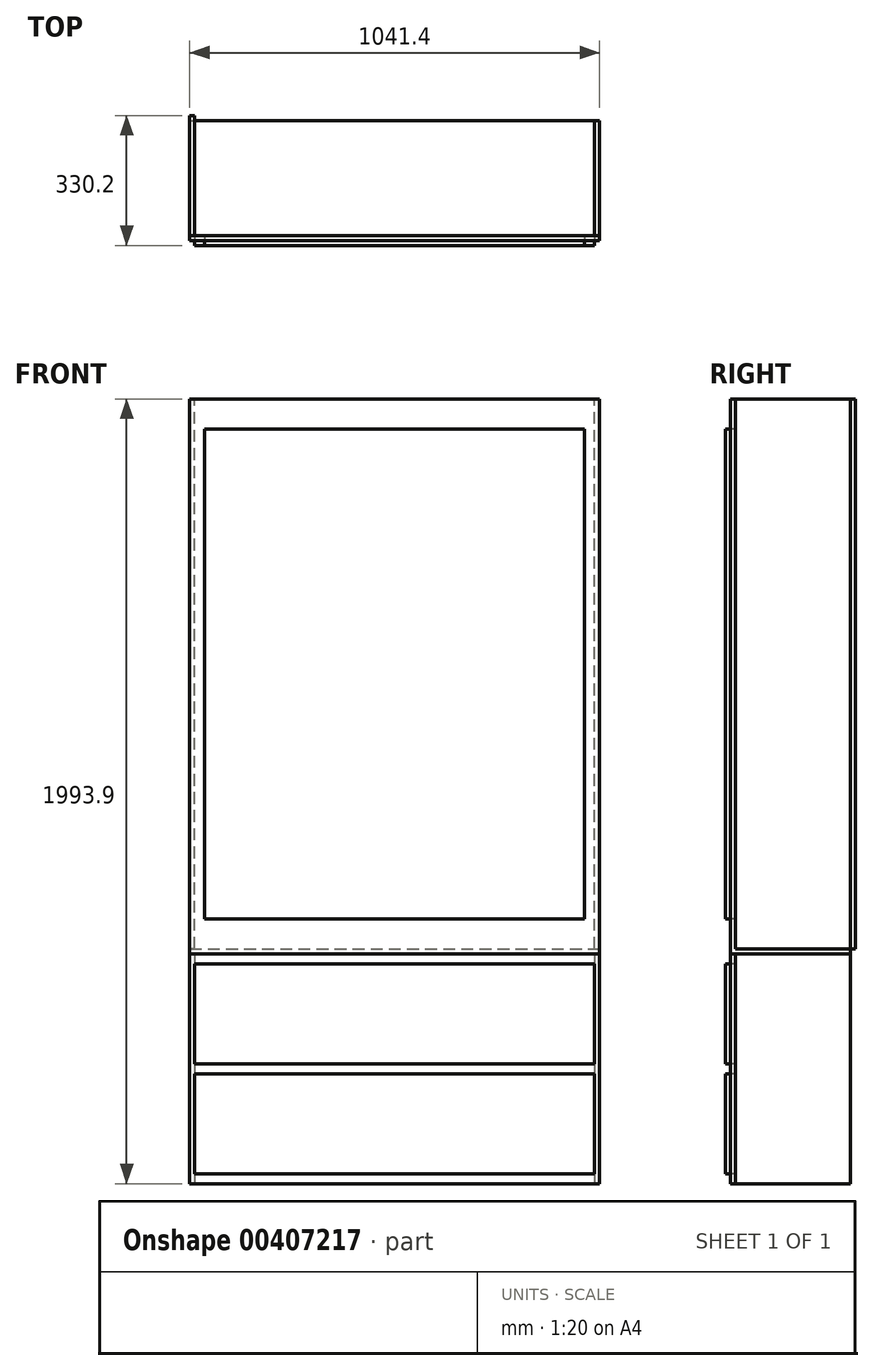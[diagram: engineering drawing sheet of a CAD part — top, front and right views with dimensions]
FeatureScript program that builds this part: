
annotation { "Feature Type Name" : "Feature", "Feature Type Description" : "" }
export const myFeature = defineFeature(function(context is Context, id is Id, definition is map)
    precondition{}
    {
        {
            var Q0;
            Q0=qCreatedBy(makeId("Front.planeOp"),FACE);
            var sketch = newSketch(context, id + "F0", { "sketchPlane" : qUnion([Q0])});
            skLineSegment(sketch, "E0.bottom", {"start": v(0, 839) * mm, "end": v(-482.6, 839) * mm});
            skLineSegment(sketch, "E0.top", {"start": v(0, -405.6) * mm, "end": v(-482.6, -405.6) * mm});
            skLineSegment(sketch, "E0.left", {"start": v(0, 839) * mm, "end": v(0, -405.6) * mm});
            skLineSegment(sketch, "E0.right", {"start": v(-482.6, 839) * mm, "end": v(-482.6, -405.6) * mm});
            skSolve(sketch);
        }
        {
            var Q0;
            Q0=makeQuery(id+"F0.imprint","IMPRINT",FACE,{"disambiguationData":[TD([[makeQuery(id+"F0.imprint","IMPRINT",EDGE,{"derivedFrom":sQuery(id+"F0.wireOp",EDGE,"E0.bottom")}),1.0]])]});
            extrude(context, id + "F1", {"entities" : qUnion([Q0]), "depth" : 12.7 * mm});
        }
        {
            var Q0;
            Q0=qCreatedBy(makeId("Front.planeOp"),FACE);
            var sketch = newSketch(context, id + "F2", { "sketchPlane" : qUnion([Q0])});
            skLineSegment(sketch, "E1.bottom", {"start": v(122.25, 18.6) * mm, "end": v(1138.25, 18.6) * mm});
            skLineSegment(sketch, "E1.top", {"start": v(122.25, -311.6) * mm, "end": v(1138.25, -311.6) * mm});
            skLineSegment(sketch, "E1.left", {"start": v(122.25, 18.6) * mm, "end": v(122.25, -311.6) * mm});
            skLineSegment(sketch, "E1.right", {"start": v(1138.25, 18.6) * mm, "end": v(1138.25, -311.6) * mm});
            skSolve(sketch);
        }
        {
            var Q0;
            Q0=makeQuery(id+"F2.imprint","IMPRINT",FACE,{"disambiguationData":[TD([[makeQuery(id+"F2.imprint","IMPRINT",EDGE,{"derivedFrom":sQuery(id+"F2.wireOp",EDGE,"E1.bottom")}),-1.0]])]});
            extrude(context, id + "F3", {"entities" : qUnion([Q0]), "depth" : 12.7 * mm});
        }
        {
            var Q0;
            Q0=qCreatedBy(makeId("Front.planeOp"),FACE);
            var sketch = newSketch(context, id + "F4", { "sketchPlane" : qUnion([Q0])});
            skLineSegment(sketch, "E2.bottom", {"start": v(525.46, 1708.69) * mm, "end": v(779.46, 1708.69) * mm});
            skLineSegment(sketch, "E2.top", {"start": v(525.46, 692.69) * mm, "end": v(779.46, 692.69) * mm});
            skLineSegment(sketch, "E2.left", {"start": v(525.46, 1708.69) * mm, "end": v(525.46, 692.69) * mm});
            skLineSegment(sketch, "E2.right", {"start": v(779.46, 1708.69) * mm, "end": v(779.46, 692.69) * mm});
            skSolve(sketch);
        }
        {
            var Q0;
            Q0=makeQuery(id+"F4.imprint","IMPRINT",FACE,{"disambiguationData":[TD([[makeQuery(id+"F4.imprint","IMPRINT",EDGE,{"derivedFrom":sQuery(id+"F4.wireOp",EDGE,"E2.bottom")}),-1.0]])]});
            extrude(context, id + "F5", {"entities" : qUnion([Q0]), "depth" : 12.7 * mm});
        }
        {
            var Q0;
            Q0=makeQuery(id+"F5.opExtrude","SWEPT_BODY",BODY,{"disambiguationData":[OSD([sQuery(id+"F4.wireOp",EDGE,"E2.bottom"),sQuery(id+"F4.wireOp",EDGE,"E2.top"),sQuery(id+"F4.wireOp",EDGE,"E2.left"),sQuery(id+"F4.wireOp",EDGE,"E2.right")])]});
            deleteBodies(context, id + "F6", {"entities" : qUnion([Q0])});
        }
        {
            var Q0;
            Q0=makeQuery(id+"F3.opExtrude","SWEPT_BODY",BODY,{"disambiguationData":[OSD([sQuery(id+"F2.wireOp",EDGE,"E1.bottom"),sQuery(id+"F2.wireOp",EDGE,"E1.top"),sQuery(id+"F2.wireOp",EDGE,"E1.left"),sQuery(id+"F2.wireOp",EDGE,"E1.right")])]});
            deleteBodies(context, id + "F7", {"entities" : qUnion([Q0])});
        }
        {
            var Q0;
            Q0=makeQuery(id+"F1.opExtrude","SWEPT_BODY",BODY,{"disambiguationData":[OSD([sQuery(id+"F0.wireOp",EDGE,"E0.bottom"),sQuery(id+"F0.wireOp",EDGE,"E0.top"),sQuery(id+"F0.wireOp",EDGE,"E0.left"),sQuery(id+"F0.wireOp",EDGE,"E0.right")])]});
            deleteBodies(context, id + "F8", {"entities" : qUnion([Q0])});
        }
        {
            var Q0;
            Q0=qCreatedBy(makeId("Front.planeOp"),FACE);
            var sketch = newSketch(context, id + "F9", { "sketchPlane" : qUnion([Q0])});
            skLineSegment(sketch, "E3.bottom", {"start": v(-520.7, -410.94) * mm, "end": v(520.7, -410.94) * mm});
            skLineSegment(sketch, "E3.top", {"start": v(-520.7, -423.64) * mm, "end": v(520.7, -423.64) * mm});
            skLineSegment(sketch, "E3.left", {"start": v(-520.7, -410.94) * mm, "end": v(-520.7, -423.64) * mm});
            skLineSegment(sketch, "E3.right", {"start": v(520.7, -410.94) * mm, "end": v(520.7, -423.64) * mm});
            skSolve(sketch);
        }
        {
            var Q0;
            Q0=qCreatedBy(makeId("Front.planeOp"),FACE);
            var sketch = newSketch(context, id + "F10", { "sketchPlane" : qUnion([Q0])});
            skLineSegment(sketch, "E4.bottom", {"start": v(-520.7, -423.64) * mm, "end": v(520.7, -423.64) * mm});
            skLineSegment(sketch, "E4.top", {"start": v(-520.7, -449.04) * mm, "end": v(520.7, -449.04) * mm});
            skLineSegment(sketch, "E4.left", {"start": v(-520.7, -423.64) * mm, "end": v(-520.7, -449.04) * mm});
            skLineSegment(sketch, "E4.right", {"start": v(520.7, -423.64) * mm, "end": v(520.7, -449.04) * mm});
            skSolve(sketch);
        }
        {
            var Q0;
            Q0=qCreatedBy(makeId("Front.planeOp"),FACE);
            var sketch = newSketch(context, id + "F11", { "sketchPlane" : qUnion([Q0])});
            skLineSegment(sketch, "E5.bottom", {"start": v(-520.7, -449.04) * mm, "end": v(-508, -449.04) * mm});
            skLineSegment(sketch, "E5.top", {"start": v(-520.7, -1007.84) * mm, "end": v(-508, -1007.84) * mm});
            skLineSegment(sketch, "E5.left", {"start": v(-520.7, -449.04) * mm, "end": v(-520.7, -1007.84) * mm});
            skLineSegment(sketch, "E5.right", {"start": v(-508, -449.04) * mm, "end": v(-508, -1007.84) * mm});
            skSolve(sketch);
        }
        {
            var Q0;
            Q0=qCreatedBy(makeId("Front.planeOp"),FACE);
            var sketch = newSketch(context, id + "F12", { "sketchPlane" : qUnion([Q0])});
            skLineSegment(sketch, "E6.bottom", {"start": v(520.7, -449.04) * mm, "end": v(508, -449.04) * mm});
            skLineSegment(sketch, "E6.top", {"start": v(520.7, -1007.84) * mm, "end": v(508, -1007.84) * mm});
            skLineSegment(sketch, "E6.left", {"start": v(520.7, -449.04) * mm, "end": v(520.7, -1007.84) * mm});
            skLineSegment(sketch, "E6.right", {"start": v(508, -449.04) * mm, "end": v(508, -1007.84) * mm});
            skSolve(sketch);
        }
        {
            var Q0;
            Q0=qCreatedBy(makeId("Front.planeOp"),FACE);
            var sketch = newSketch(context, id + "F13", { "sketchPlane" : qUnion([Q0])});
            skLineSegment(sketch, "E7.bottom", {"start": v(-508, -449.04) * mm, "end": v(508, -449.04) * mm});
            skLineSegment(sketch, "E7.top", {"start": v(-508, -703.04) * mm, "end": v(508, -703.04) * mm});
            skLineSegment(sketch, "E7.left", {"start": v(-508, -449.04) * mm, "end": v(-508, -703.04) * mm});
            skLineSegment(sketch, "E7.right", {"start": v(508, -449.04) * mm, "end": v(508, -703.04) * mm});
            skSolve(sketch);
        }
        {
            var Q0;
            Q0=qCreatedBy(makeId("Front.planeOp"),FACE);
            var sketch = newSketch(context, id + "F14", { "sketchPlane" : qUnion([Q0])});
            skLineSegment(sketch, "E8.bottom", {"start": v(-508, -703.04) * mm, "end": v(508, -703.04) * mm});
            skLineSegment(sketch, "E8.top", {"start": v(-508, -728.44) * mm, "end": v(508, -728.44) * mm});
            skLineSegment(sketch, "E8.left", {"start": v(-508, -703.04) * mm, "end": v(-508, -728.44) * mm});
            skLineSegment(sketch, "E8.right", {"start": v(508, -703.04) * mm, "end": v(508, -728.44) * mm});
            skSolve(sketch);
        }
        {
            var Q0;
            Q0=qCreatedBy(makeId("Front.planeOp"),FACE);
            var sketch = newSketch(context, id + "F15", { "sketchPlane" : qUnion([Q0])});
            skLineSegment(sketch, "E9.bottom", {"start": v(-508, -728.44) * mm, "end": v(508, -728.44) * mm});
            skLineSegment(sketch, "E9.top", {"start": v(-508, -982.44) * mm, "end": v(508, -982.44) * mm});
            skLineSegment(sketch, "E9.left", {"start": v(-508, -728.44) * mm, "end": v(-508, -982.44) * mm});
            skLineSegment(sketch, "E9.right", {"start": v(508, -728.44) * mm, "end": v(508, -982.44) * mm});
            skSolve(sketch);
        }
        {
            var Q0;
            Q0=qCreatedBy(makeId("Front.planeOp"),FACE);
            var sketch = newSketch(context, id + "F16", { "sketchPlane" : qUnion([Q0])});
            skLineSegment(sketch, "E10.bottom", {"start": v(-508, -982.44) * mm, "end": v(508, -982.44) * mm});
            skLineSegment(sketch, "E10.top", {"start": v(-508, -1007.84) * mm, "end": v(508, -1007.84) * mm});
            skLineSegment(sketch, "E10.left", {"start": v(-508, -982.44) * mm, "end": v(-508, -1007.84) * mm});
            skLineSegment(sketch, "E10.right", {"start": v(508, -982.44) * mm, "end": v(508, -1007.84) * mm});
            skSolve(sketch);
        }
        {
            var Q0;
            Q0=qCreatedBy(makeId("Front.planeOp"),FACE);
            var sketch = newSketch(context, id + "F17", { "sketchPlane" : qUnion([Q0])});
            skLineSegment(sketch, "E11.bottom", {"start": v(-482.6, -410.94) * mm, "end": v(482.6, -410.94) * mm});
            skLineSegment(sketch, "E11.top", {"start": v(-482.6, -334.74) * mm, "end": v(482.6, -334.74) * mm});
            skLineSegment(sketch, "E11.left", {"start": v(-482.6, -410.94) * mm, "end": v(-482.6, -334.74) * mm});
            skLineSegment(sketch, "E11.right", {"start": v(482.6, -410.94) * mm, "end": v(482.6, -334.74) * mm});
            skSolve(sketch);
        }
        {
            var Q0;
            Q0=qCreatedBy(makeId("Front.planeOp"),FACE);
            var sketch = newSketch(context, id + "F18", { "sketchPlane" : qUnion([Q0])});
            skLineSegment(sketch, "E12.bottom", {"start": v(-482.6, 909.86) * mm, "end": v(0, 909.86) * mm});
            skLineSegment(sketch, "E12.top", {"start": v(-482.6, -334.74) * mm, "end": v(0, -334.74) * mm});
            skLineSegment(sketch, "E12.left", {"start": v(-482.6, 909.86) * mm, "end": v(-482.6, -334.74) * mm});
            skLineSegment(sketch, "E12.right", {"start": v(0, 909.86) * mm, "end": v(0, -334.74) * mm});
            skSolve(sketch);
        }
        {
            var Q0;
            Q0=qCreatedBy(makeId("Front.planeOp"),FACE);
            var sketch = newSketch(context, id + "F19", { "sketchPlane" : qUnion([Q0])});
            skLineSegment(sketch, "E13.bottom", {"start": v(482.6, -334.74) * mm, "end": v(0, -334.74) * mm});
            skLineSegment(sketch, "E13.top", {"start": v(482.6, 909.86) * mm, "end": v(0, 909.86) * mm});
            skLineSegment(sketch, "E13.left", {"start": v(482.6, -334.74) * mm, "end": v(482.6, 909.86) * mm});
            skLineSegment(sketch, "E13.right", {"start": v(0, -334.74) * mm, "end": v(0, 909.86) * mm});
            skSolve(sketch);
        }
        {
            var Q0;
            Q0=qCreatedBy(makeId("Front.planeOp"),FACE);
            var sketch = newSketch(context, id + "F20", { "sketchPlane" : qUnion([Q0])});
            skLineSegment(sketch, "E14.bottom", {"start": v(-482.6, -410.94) * mm, "end": v(-520.7, -410.94) * mm});
            skLineSegment(sketch, "E14.top", {"start": v(-482.6, 909.86) * mm, "end": v(-520.7, 909.86) * mm});
            skLineSegment(sketch, "E14.left", {"start": v(-482.6, -410.94) * mm, "end": v(-482.6, 909.86) * mm});
            skLineSegment(sketch, "E14.right", {"start": v(-520.7, -410.94) * mm, "end": v(-520.7, 909.86) * mm});
            skSolve(sketch);
        }
        {
            var Q0;
            Q0=qCreatedBy(makeId("Front.planeOp"),FACE);
            var sketch = newSketch(context, id + "F21", { "sketchPlane" : qUnion([Q0])});
            skLineSegment(sketch, "E15.bottom", {"start": v(482.6, 909.86) * mm, "end": v(520.7, 909.86) * mm});
            skLineSegment(sketch, "E15.top", {"start": v(482.6, -410.94) * mm, "end": v(520.7, -410.94) * mm});
            skLineSegment(sketch, "E15.left", {"start": v(482.6, 909.86) * mm, "end": v(482.6, -410.94) * mm});
            skLineSegment(sketch, "E15.right", {"start": v(520.7, 909.86) * mm, "end": v(520.7, -410.94) * mm});
            skSolve(sketch);
        }
        {
            var Q0;
            Q0=qCreatedBy(makeId("Front.planeOp"),FACE);
            var sketch = newSketch(context, id + "F22", { "sketchPlane" : qUnion([Q0])});
            skLineSegment(sketch, "E16.bottom", {"start": v(-520.7, 909.86) * mm, "end": v(520.7, 909.86) * mm});
            skLineSegment(sketch, "E16.top", {"start": v(-520.7, 986.06) * mm, "end": v(520.7, 986.06) * mm});
            skLineSegment(sketch, "E16.left", {"start": v(-520.7, 909.86) * mm, "end": v(-520.7, 986.06) * mm});
            skLineSegment(sketch, "E16.right", {"start": v(520.7, 909.86) * mm, "end": v(520.7, 986.06) * mm});
            skSolve(sketch);
        }
        {
            var Q0;
            Q0=makeQuery(id+"F15.imprint","IMPRINT",FACE,{"disambiguationData":[TD([[makeQuery(id+"F15.imprint","IMPRINT",EDGE,{"derivedFrom":sQuery(id+"F15.wireOp",EDGE,"E9.bottom")}),-1.0]])]});
            var Q1;
            Q1=makeQuery(id+"F13.imprint","IMPRINT",FACE,{"disambiguationData":[TD([[makeQuery(id+"F13.imprint","IMPRINT",EDGE,{"derivedFrom":sQuery(id+"F13.wireOp",EDGE,"E7.bottom")}),-1.0]])]});
            var Q2;
            Q2=makeQuery(id+"F18.imprint","IMPRINT",FACE,{"disambiguationData":[TD([[makeQuery(id+"F18.imprint","IMPRINT",EDGE,{"derivedFrom":sQuery(id+"F18.wireOp",EDGE,"E12.bottom")}),-1.0]])]});
            var Q3;
            Q3=makeQuery(id+"F19.imprint","IMPRINT",FACE,{"disambiguationData":[TD([[makeQuery(id+"F19.imprint","IMPRINT",EDGE,{"derivedFrom":sQuery(id+"F19.wireOp",EDGE,"E13.bottom")}),-1.0]])]});
            extrude(context, id + "F23", {"entities" : qUnion([Q0, Q1, Q2, Q3]), "depth" : 12.7 * mm});
        }
        {
            var Q0;
            Q0=makeQuery(id+"F10.imprint","IMPRINT",FACE,{"disambiguationData":[TD([[makeQuery(id+"F10.imprint","IMPRINT",EDGE,{"derivedFrom":sQuery(id+"F10.wireOp",EDGE,"E4.bottom")}),-1.0]])]});
            var Q1;
            Q1=makeQuery(id+"F17.imprint","IMPRINT",FACE,{"disambiguationData":[TD([[makeQuery(id+"F17.imprint","IMPRINT",EDGE,{"derivedFrom":sQuery(id+"F17.wireOp",EDGE,"E11.bottom")}),1.0]])]});
            var Q2;
            Q2=makeQuery(id+"F14.imprint","IMPRINT",FACE,{"disambiguationData":[TD([[makeQuery(id+"F14.imprint","IMPRINT",EDGE,{"derivedFrom":sQuery(id+"F14.wireOp",EDGE,"E8.bottom")}),-1.0]])]});
            var Q3;
            Q3=makeQuery(id+"F16.imprint","IMPRINT",FACE,{"disambiguationData":[TD([[makeQuery(id+"F16.imprint","IMPRINT",EDGE,{"derivedFrom":sQuery(id+"F16.wireOp",EDGE,"E10.bottom")}),-1.0]])]});
            extrude(context, id + "F24", {"entities" : qUnion([Q0, Q1, Q2, Q3]), "oppositeDirection" : true, "depth" : 12.7 * mm});
        }
        {
            var Q0;
            Q0=makeQuery(id+"F22.imprint","IMPRINT",FACE,{"disambiguationData":[TD([[makeQuery(id+"F22.imprint","IMPRINT",EDGE,{"derivedFrom":sQuery(id+"F22.wireOp",EDGE,"E16.bottom")}),1.0]])]});
            extrude(context, id + "F25", {"entities" : qUnion([Q0]), "oppositeDirection" : true, "depth" : 12.7 * mm});
        }
        {
            var Q0;
            Q0=makeQuery(id+"F9.imprint","IMPRINT",FACE,{"disambiguationData":[TD([[makeQuery(id+"F9.imprint","IMPRINT",EDGE,{"derivedFrom":sQuery(id+"F9.wireOp",EDGE,"E3.bottom")}),-1.0]])]});
            extrude(context, id + "F26", {"entities" : qUnion([Q0]), "oppositeDirection" : true, "depth" : 304.8 * mm});
        }
        {
            var Q0;
            Q0=makeQuery(id+"F12.imprint","IMPRINT",FACE,{"disambiguationData":[TD([[makeQuery(id+"F12.imprint","IMPRINT",EDGE,{"derivedFrom":sQuery(id+"F12.wireOp",EDGE,"E6.bottom")}),1.0]])]});
            var Q1;
            Q1=makeQuery(id+"F11.imprint","IMPRINT",FACE,{"disambiguationData":[TD([[makeQuery(id+"F11.imprint","IMPRINT",EDGE,{"derivedFrom":sQuery(id+"F11.wireOp",EDGE,"E5.bottom")}),-1.0]])]});
            var Q2;
            Q2=makeQuery(id+"F20.imprint","IMPRINT",FACE,{"disambiguationData":[TD([[makeQuery(id+"F20.imprint","IMPRINT",EDGE,{"derivedFrom":sQuery(id+"F20.wireOp",EDGE,"E14.bottom")}),-1.0]])]});
            var Q3;
            Q3=makeQuery(id+"F21.imprint","IMPRINT",FACE,{"disambiguationData":[TD([[makeQuery(id+"F21.imprint","IMPRINT",EDGE,{"derivedFrom":sQuery(id+"F21.wireOp",EDGE,"E15.bottom")}),-1.0]])]});
            extrude(context, id + "F27", {"entities" : qUnion([Q0, Q1, Q2, Q3]), "operationType" : NewBodyOperationType.ADD, "oppositeDirection" : true, "depth" : 12.7 * mm});
        }
        {
            var Q0;
            Q0=makeQuery(id+"F24.opExtrude","SWEPT_FACE",FACE,{"disambiguationData":[OSD([sQuery(id+"F10.wireOp",EDGE,"E4.right")])]});
            var sketch = newSketch(context, id + "F28", { "sketchPlane" : qUnion([Q0])});
            skLineSegment(sketch, "E17.bottom", {"start": v(12.7, -423.64) * mm, "end": v(304.8, -423.64) * mm});
            skLineSegment(sketch, "E17.top", {"start": v(12.7, -1007.84) * mm, "end": v(304.8, -1007.84) * mm});
            skLineSegment(sketch, "E17.left", {"start": v(12.7, -423.64) * mm, "end": v(12.7, -1007.84) * mm});
            skLineSegment(sketch, "E17.right", {"start": v(304.8, -423.64) * mm, "end": v(304.8, -1007.84) * mm});
            skSolve(sketch);
        }
        {
            var Q0;
            {var subQ4=sQuery(id+"F28.wireOp",EDGE,"E17.bottom");Q0=makeQuery(id+"F28.imprint","IMPRINT",FACE,{"disambiguationData":[TD([[makeQuery(id+"F28.imprint","IMPRINT",EDGE,{"derivedFrom":subQ4}),-1.0]])]});}
            extrude(context, id + "F29", {"entities" : qUnion([Q0]), "oppositeDirection" : true, "depth" : 12.7 * mm});
        }
        {
            var Q0;
            Q0=makeQuery(id+"F24.opExtrude","SWEPT_FACE",FACE,{"disambiguationData":[OSD([sQuery(id+"F10.wireOp",EDGE,"E4.left")])]});
            var sketch = newSketch(context, id + "F30", { "sketchPlane" : qUnion([Q0])});
            skLineSegment(sketch, "E18.bottom", {"start": v(-12.7, -423.64) * mm, "end": v(-304.8, -423.64) * mm});
            skLineSegment(sketch, "E18.top", {"start": v(-12.7, -1007.84) * mm, "end": v(-304.8, -1007.84) * mm});
            skLineSegment(sketch, "E18.left", {"start": v(-12.7, -423.64) * mm, "end": v(-12.7, -1007.84) * mm});
            skLineSegment(sketch, "E18.right", {"start": v(-304.8, -423.64) * mm, "end": v(-304.8, -1007.84) * mm});
            skSolve(sketch);
        }
        {
            var Q0;
            {var subQ1=sQuery(id+"F30.wireOp",EDGE,"E18.bottom");Q0=makeQuery(id+"F30.imprint","IMPRINT",FACE,{"disambiguationData":[TD([[makeQuery(id+"F30.imprint","IMPRINT",EDGE,{"derivedFrom":subQ1}),1.0]])]});}
            extrude(context, id + "F31", {"entities" : qUnion([Q0]), "oppositeDirection" : true, "depth" : 12.7 * mm});
        }
        {
            var Q0;
            Q0=makeQuery(id+"F25.opExtrude","SWEPT_FACE",FACE,{"disambiguationData":[OSD([sQuery(id+"F22.wireOp",EDGE,"E16.left")])]});
            var sketch = newSketch(context, id + "F32", { "sketchPlane" : qUnion([Q0])});
            skLineSegment(sketch, "E19.bottom", {"start": v(-12.7, 986.06) * mm, "end": v(-317.5, 986.06) * mm});
            skLineSegment(sketch, "E19.top", {"start": v(-12.7, -410.94) * mm, "end": v(-317.5, -410.94) * mm});
            skLineSegment(sketch, "E19.left", {"start": v(-12.7, 986.06) * mm, "end": v(-12.7, -410.94) * mm});
            skLineSegment(sketch, "E19.right", {"start": v(-317.5, 986.06) * mm, "end": v(-317.5, -410.94) * mm});
            skSolve(sketch);
        }
        {
            var Q0;
            {var subQ4=sQuery(id+"F32.wireOp",EDGE,"E19.bottom");Q0=makeQuery(id+"F32.imprint","IMPRINT",FACE,{"disambiguationData":[TD([[makeQuery(id+"F32.imprint","IMPRINT",EDGE,{"derivedFrom":subQ4}),1.0]])]});}
            extrude(context, id + "F33", {"entities" : qUnion([Q0]), "oppositeDirection" : true, "depth" : 12.7 * mm});
        }
        {
            var Q0;
            Q0=makeQuery(id+"F25.opExtrude","SWEPT_FACE",FACE,{"disambiguationData":[OSD([sQuery(id+"F22.wireOp",EDGE,"E16.right")])]});
            var sketch = newSketch(context, id + "F34", { "sketchPlane" : qUnion([Q0])});
            skLineSegment(sketch, "E20.bottom", {"start": v(12.7, 986.06) * mm, "end": v(304.8, 986.06) * mm});
            skLineSegment(sketch, "E20.top", {"start": v(12.7, -410.94) * mm, "end": v(304.8, -410.94) * mm});
            skLineSegment(sketch, "E20.left", {"start": v(12.7, 986.06) * mm, "end": v(12.7, -410.94) * mm});
            skLineSegment(sketch, "E20.right", {"start": v(304.8, 986.06) * mm, "end": v(304.8, -410.94) * mm});
            skSolve(sketch);
        }
        {
            var Q0;
            {var subQ4=sQuery(id+"F34.wireOp",EDGE,"E20.bottom");Q0=makeQuery(id+"F34.imprint","IMPRINT",FACE,{"disambiguationData":[TD([[makeQuery(id+"F34.imprint","IMPRINT",EDGE,{"derivedFrom":subQ4}),-1.0]])]});}
            extrude(context, id + "F35", {"entities" : qUnion([Q0]), "oppositeDirection" : true, "depth" : 12.7 * mm});
        }
    });
